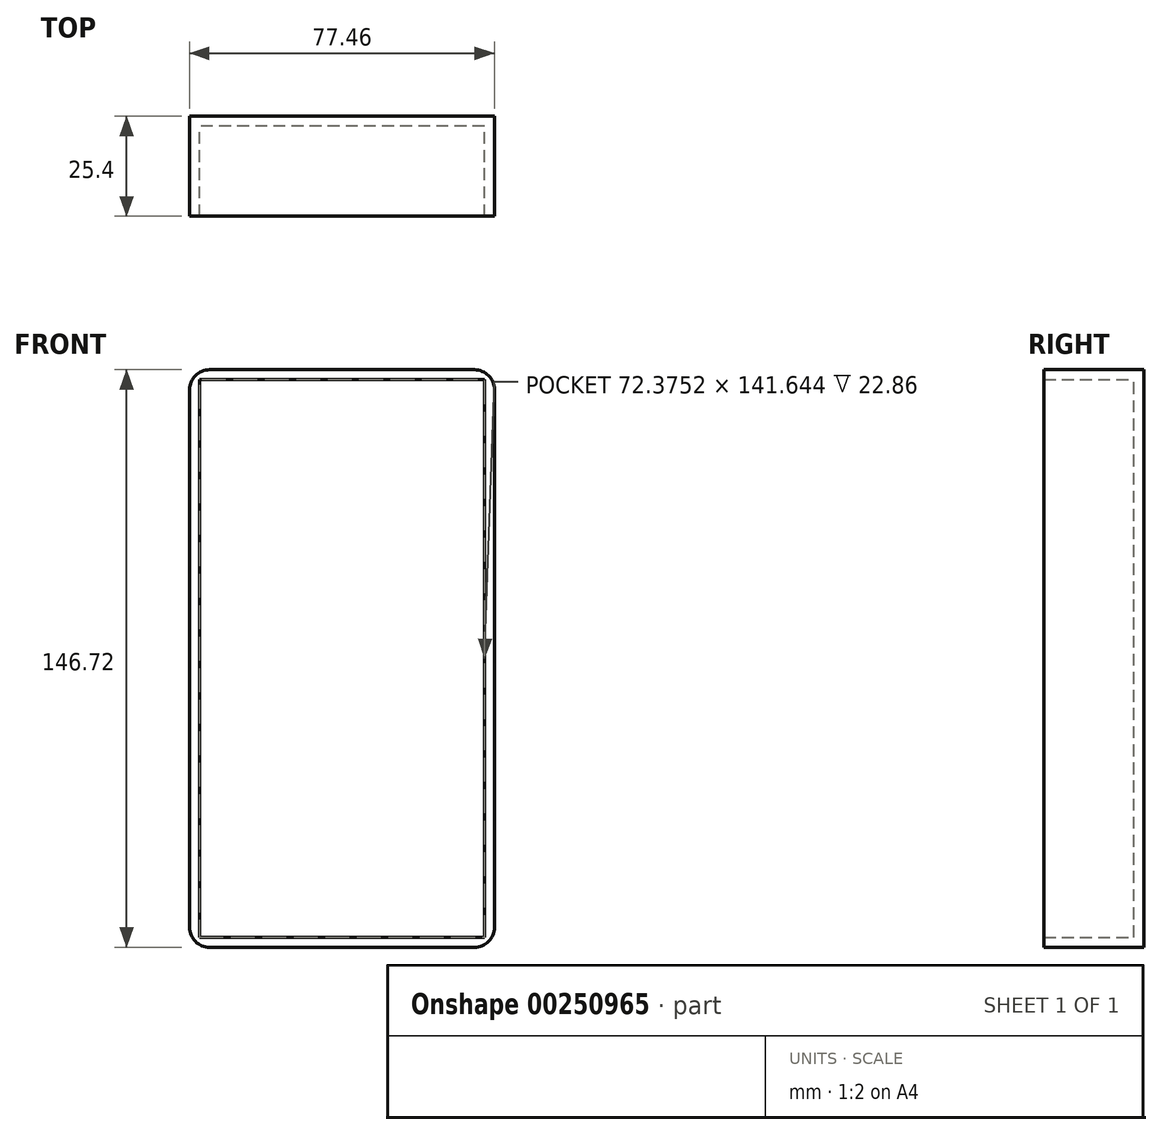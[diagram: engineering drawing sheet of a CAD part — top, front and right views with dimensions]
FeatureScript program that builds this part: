
annotation { "Feature Type Name" : "Feature", "Feature Type Description" : "" }
export const myFeature = defineFeature(function(context is Context, id is Id, definition is map)
    precondition{}
    {
        {
            var Q0;
            Q0=qCreatedBy(makeId("Front.planeOp"),FACE);
            var sketch = newSketch(context, id + "F0", { "sketchPlane" : qUnion([Q0])});
            skLineSegment(sketch, "E0.bottom", {"start": v(38.73, -73.36) * mm, "end": v(-38.73, -73.36) * mm});
            skLineSegment(sketch, "E0.top", {"start": v(38.73, 73.36) * mm, "end": v(-38.73, 73.36) * mm});
            skLineSegment(sketch, "E0.left", {"start": v(38.73, -73.36) * mm, "end": v(38.73, 73.36) * mm});
            skLineSegment(sketch, "E0.right", {"start": v(-38.73, -73.36) * mm, "end": v(-38.73, 73.36) * mm});
            skPoint(sketch, "E0.middle", {"position": v(0, 0) * mm});
            skSolve(sketch);
        }
        {
            var Q0;
            Q0 = qSketchRegion(id + "F0", true);
            extrude(context, id + "F1", {"entities" : qUnion([Q0]), "endBound" : BoundingType.SYMMETRIC, "depth" : 25.4 * mm});
        }
        {
            var Q0;
            Q0=makeQuery(id+"F1.opExtrude","CAP_FACE",FACE,{"disambiguationData":[OSD([sQuery(id+"F0.wireOp",EDGE,"E0.bottom"),sQuery(id+"F0.wireOp",EDGE,"E0.top"),sQuery(id+"F0.wireOp",EDGE,"E0.left"),sQuery(id+"F0.wireOp",EDGE,"E0.right")])],"isStart":false});
            shell(context, id + "F2", {"entities" : qUnion([Q0]), "thickness" : 2.54 * mm});
        }
        {
            var Q0;
            Q0=makeQuery(id+"F1.opExtrude","SWEPT_EDGE",EDGE,{"disambiguationData":[OSD([sQuery(id+"F0.wireOp",EDGE,"E0.top"),sQuery(id+"F0.wireOp",EDGE,"E0.left")])]});
            var Q1;
            Q1=makeQuery(id+"F1.opExtrude","SWEPT_EDGE",EDGE,{"disambiguationData":[OSD([sQuery(id+"F0.wireOp",EDGE,"E0.bottom"),sQuery(id+"F0.wireOp",EDGE,"E0.left")])]});
            var Q2;
            Q2=makeQuery(id+"F1.opExtrude","SWEPT_EDGE",EDGE,{"disambiguationData":[OSD([sQuery(id+"F0.wireOp",EDGE,"E0.top"),sQuery(id+"F0.wireOp",EDGE,"E0.right")])]});
            var Q3;
            Q3=makeQuery(id+"F1.opExtrude","SWEPT_EDGE",EDGE,{"disambiguationData":[OSD([sQuery(id+"F0.wireOp",EDGE,"E0.bottom"),sQuery(id+"F0.wireOp",EDGE,"E0.right")])]});
            fillet(context, id + "F3", {"entities" : qUnion([Q0, Q1, Q2, Q3]), "radius" : 5.08 * mm, "tangentPropagation" : true, "allowEdgeOverflow" : false});
        }
    });
